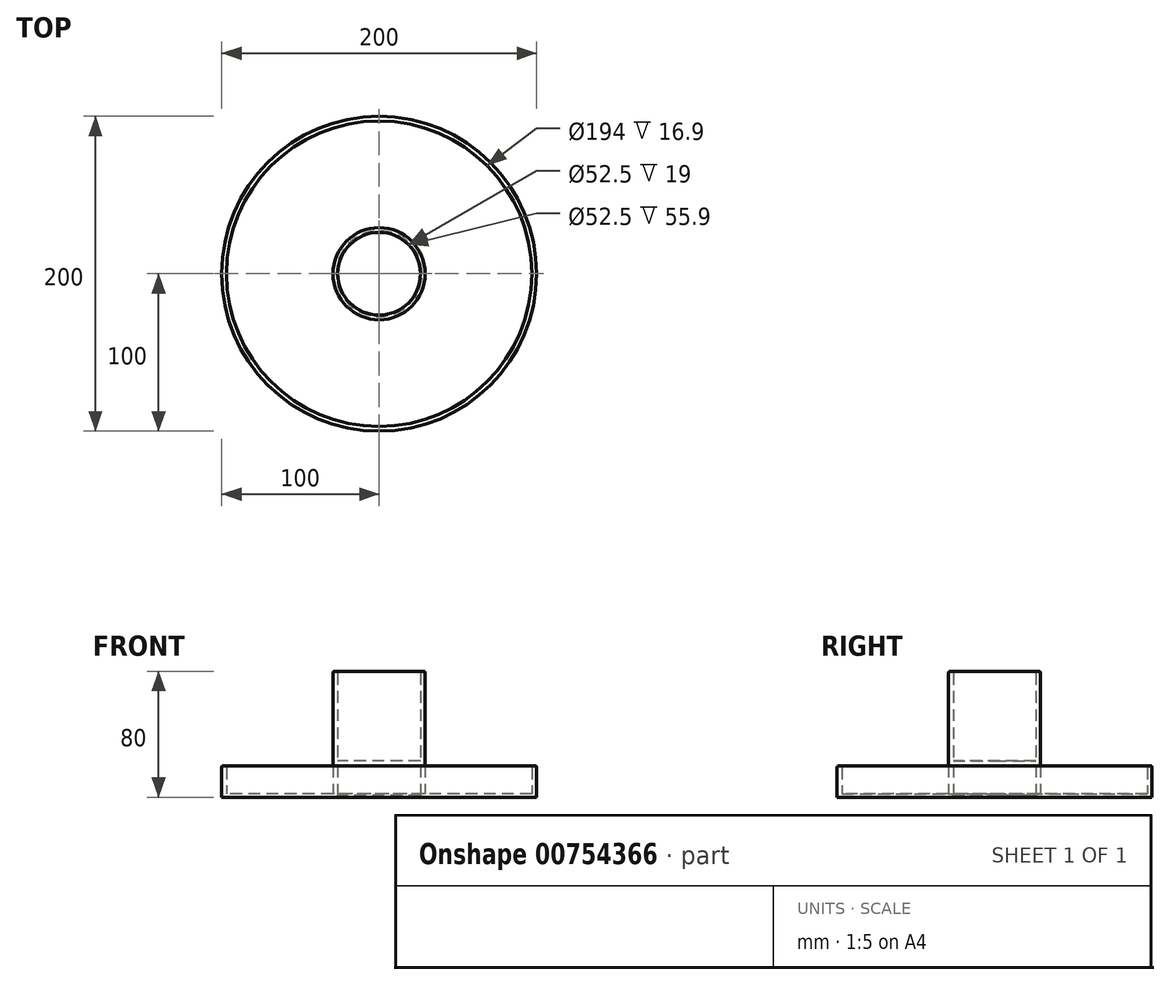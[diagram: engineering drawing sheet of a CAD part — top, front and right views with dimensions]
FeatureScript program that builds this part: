
annotation { "Feature Type Name" : "Feature", "Feature Type Description" : "" }
export const myFeature = defineFeature(function(context is Context, id is Id, definition is map)
    precondition{}
    {
        {
            var Q0;
            Q0=qCreatedBy(makeId("Top.planeOp"),FACE);
            var sketch = newSketch(context, id + "F0", { "sketchPlane" : qUnion([Q0])});
            skCircle(sketch, "E0", {"center": v(0, 0) * mm, "radius": 100 * mm});
            skCircle(sketch, "E1.0", {"center": v(0, 0) * mm, "radius": 97 * mm});
            skCircle(sketch, "E2", {"center": v(0, 0) * mm, "radius": 26.25 * mm});
            skCircle(sketch, "E3.0", {"center": v(0, 0) * mm, "radius": 29.25 * mm});
            skSolve(sketch);
        }
        {
            var Q0;
            Q0=makeQuery(id+"F0.imprint","IMPRINT",FACE,{"disambiguationData":[TD([[makeQuery(id+"F0.imprint","IMPRINT",EDGE,{"derivedFrom":sQuery(id+"F0.wireOp",EDGE,"E1.0")}),1.0]])]});
            extrude(context, id + "F1", {"entities" : qUnion([Q0]), "depth" : 2 * mm, "offsetDistance" : 25 * mm});
        }
        {
            var Q0;
            Q0=makeQuery(id+"F0.imprint","IMPRINT",FACE,{"disambiguationData":[TD([[makeQuery(id+"F0.imprint","IMPRINT",EDGE,{"derivedFrom":sQuery(id+"F0.wireOp",EDGE,"E0")}),1.0]])]});
            extrude(context, id + "F2", {"entities" : qUnion([Q0]), "operationType" : NewBodyOperationType.ADD, "depth" : 20 * mm, "offsetDistance" : 25 * mm});
        }
        {
            var Q0;
            Q0=makeQuery(id+"F0.imprint","IMPRINT",FACE,{"disambiguationData":[TD([[makeQuery(id+"F0.imprint","IMPRINT",EDGE,{"derivedFrom":sQuery(id+"F0.wireOp",EDGE,"E2")}),-1.0]])]});
            extrude(context, id + "F3", {"entities" : qUnion([Q0]), "operationType" : NewBodyOperationType.ADD, "depth" : 80 * mm, "offsetDistance" : 25 * mm});
        }
        {
            var Q0;
            Q0=makeQuery(id+"F0.imprint","IMPRINT",FACE,{"disambiguationData":[TD([[makeQuery(id+"F0.imprint","IMPRINT",EDGE,{"derivedFrom":sQuery(id+"F0.wireOp",EDGE,"E2")}),1.0]])]});
            cPlane(context, id + "F4", {"entities" : qUnion([Q0]), "cplaneType" : CPlaneType.OFFSET, "offset" : 20 * mm, "width" : 150 * mm, "height" : 150 * mm});
        }
        {
            var Q0;
            Q0=qCreatedBy(id+"F4.planeOp",FACE);
            var sketch = newSketch(context, id + "F5", { "sketchPlane" : qUnion([Q0])});
            skCircle(sketch, "E4", {"center": v(0, 0) * mm, "radius": 27.25 * mm});
            skSolve(sketch);
        }
        {
            var Q0;
            Q0=makeQuery(id+"F5.imprint","IMPRINT",FACE,{"disambiguationData":[TD([[makeQuery(id+"F5.imprint","IMPRINT",EDGE,{"derivedFrom":sQuery(id+"F5.wireOp",EDGE,"E4")}),1.0]])]});
            extrude(context, id + "F6", {"entities" : qUnion([Q0]), "operationType" : NewBodyOperationType.ADD, "depth" : 3 * mm, "offsetDistance" : 25 * mm});
        }
        {
            var Q0;
            Q0=makeQuery(id+"F2.opExtrude","CAP_EDGE",EDGE,{"disambiguationData":[OSD([sQuery(id+"F0.wireOp",EDGE,"E0")])],"isStart":false});
            var Q1;
            Q1=makeQuery(id+"F2.opExtrude","CAP_EDGE",EDGE,{"disambiguationData":[OSD([sQuery(id+"F0.wireOp",EDGE,"E1.0")])],"isStart":false});
            var Q2;
            Q2=makeQuery(id+"F3.opExtrude","CAP_EDGE",EDGE,{"disambiguationData":[OSD([sQuery(id+"F0.wireOp",EDGE,"E3.0")])],"isStart":false});
            var Q3;
            Q3=makeQuery(id+"F3.opExtrude","CAP_EDGE",EDGE,{"disambiguationData":[OSD([sQuery(id+"F0.wireOp",EDGE,"E2")])],"isStart":false});
            fillet(context, id + "F7", {"entities" : qUnion([Q0, Q1, Q2, Q3]), "radius" : 1.1 * mm, "tangentPropagation" : true, "allowEdgeOverflow" : false});
        }
        {
            var Q0;
            Q0=makeQuery(id+"F3.opExtrude","CAP_EDGE",EDGE,{"disambiguationData":[OSD([sQuery(id+"F0.wireOp",EDGE,"E2")])],"isStart":true});
            chamfer(context, id + "F8", {"entities" : qUnion([Q0]), "width" : 1 * mm, "tangentPropagation" : true});
        }
    });
